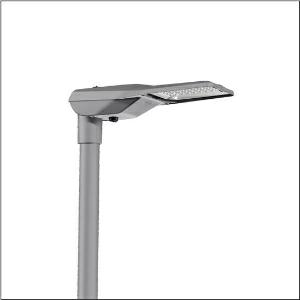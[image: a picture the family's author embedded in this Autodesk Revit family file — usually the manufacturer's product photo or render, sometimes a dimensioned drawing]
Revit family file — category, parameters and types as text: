
# Revit family: streetlight_sl_21_iq_mini___st1_0a_5xe2d31y08hb_7569
name_source: partatom
category: Lighting Fixtures
units: mm (PartAtom-declared; Revit-internal decimal feet)

## family parameters
Cut with Voids When Loaded = No
Host = Face
Light Source = No
Part Type = Normal
Room Calculation Point = No
Round Connector Dimension = Use Diameter
Shared = No

## types (1)
- --- (1 x LED, 9750 lm, 71 W, 3000K)
    Apparent Load = 71 VA
    CIE Flux Codes = 37 72 97 100 100
    Color Rendering = 70
    Color Temperature = 3000K
    Default Elevation = 1800 mm
    Description = Streetlight SL 21 iQ mini, mast luminaire, primary light control with lens, of PMMA, primary optical cover: cover, of toughened safety glass, transparent, light distribution: ST1.0a, light emission: direct distribution, primary light characteristic: asymmetric, installation type: post-top, side-entry, LED, High Power LED, rated luminous flux: 9.750lm, luminous efficacy: 137lm/W, light colour: 730, colour temperature: 3000K, control: presetting dimming logarithmic, Street-Remote, Auto-Match, Temp-Guard, Lumen-Switch, Night-Set, Smart-Wire, Light-Fading, Desk-Remote (wireless, voltage-free reading and setting of iQ features in the workshop via application-optimized NFC function/RFID function), optimised constant luminous flux control (CLO 2.0), mains connection: 220..240V, AC, 50/60Hz, start of lifetime: 71W, end of service life: 75W, reduction: 30W, luminaire housing, of diecast aluminium, powder-coated, Siteco® metallic grey (DB 702S), corrosivity category C5 mid according to DIN EN ISO 12944, please order mast flange separately, inclination adjustable: 0°, 5°, 10°, 15°, sealing non-destructively replaceable, multi-level sealing system, length: 628mm, width: 235mm, height: 110mm, mast flange for spigot size: 42mm (side-entry): 5XC10008XM4, 60/48mm (side-entry/post-top): 5XC10108XM2, 76/60mm (side-entry/post-top): 5XC10108XM1, Smart Interface below and above, protection rating (complete): IP66, insulation class (complete): insulation class II (safety insulation), certification: CE, ENEC, ENEC+, VDE, impact resistance: IK09, permissible operating ambient temperature for outdoor applications: -40..+50°C, standard-compliant lighting for roads and squares, packaging unit: 1 piece

Light Distribution: ST1.0a
    Height = 110 mm
    Lamp = 1 x LED
    Lamp Light Flux = 9750 lm
    Lamp Power = 71 W
    Lamp count = 1
    Length = 625 mm
    Luminous efficacy = 137 lm/W
    Manufacturer = Siteco
    ModVariant = No
    Model = 5XE2D31Y08HB
    Number of Poles = 1
    OnlyDefault = Yes
    Power Factor = 1
    Product Name = Streetlight SL 21 iQ mini | ST1.0a
    Product group = mast luminaire | pylon top
    ProductGroupID = 6100
    Protection Class = Protection class II
    Protection Degree = IP 66
    RLX_Detail_Level = 1
    RLX_Emergency_Light_Flux = 0 lm
    RLX_Emergency_Type = 0
    RLX_Emergency_Type_DB = No
    RlxData = <blob elided: 93481 chars, md5=ef3b4ef8>
    Socket = socket
    Standby Power = 0 W
    System Light Flux = 9750 lm
    System Power = 71 W
    Type Comments = factory setting: luminous flux: 100 % | dim-lin: 254 | 716 mA
    Type Image = l_1003514.jpg
    URL = http://relux.com
    VarID = @adj_044915
    Voltage = 0 V
    Weight = 0.00 kg
    Width = 234 mm

## geometry (parser evidence)
native form markers: Blend x4, Sweep x11
no freeform markers — native parametric forms only
